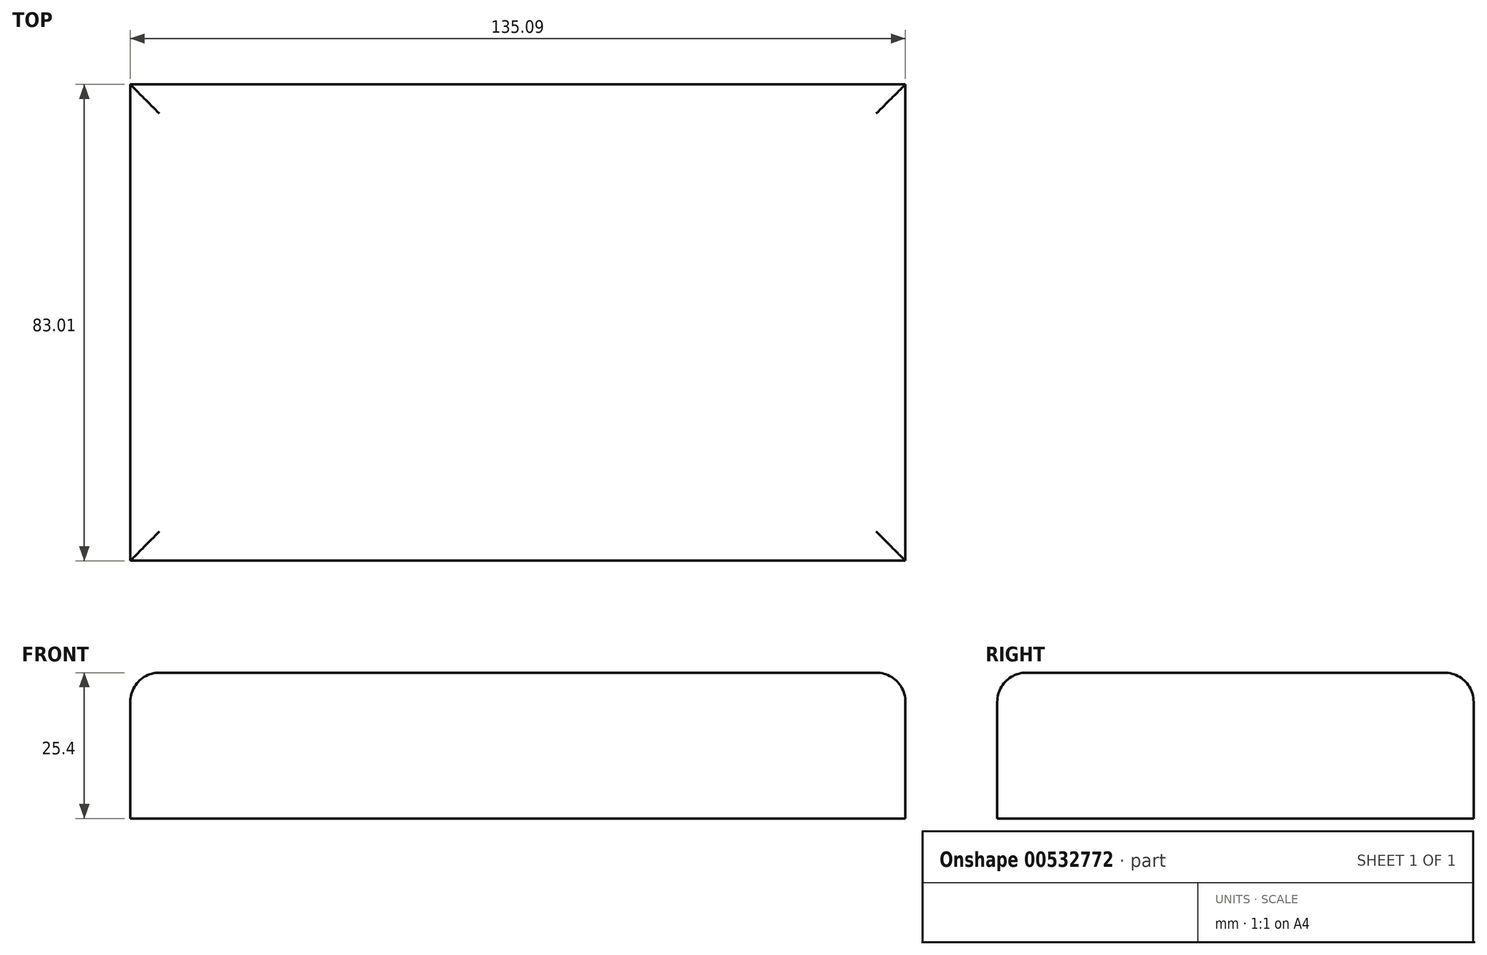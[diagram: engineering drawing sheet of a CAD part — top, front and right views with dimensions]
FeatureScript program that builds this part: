
annotation { "Feature Type Name" : "Feature", "Feature Type Description" : "" }
export const myFeature = defineFeature(function(context is Context, id is Id, definition is map)
    precondition{}
    {
        {
            var Q0;
            Q0=qCreatedBy(makeId("Top.planeOp"),FACE);
            var sketch = newSketch(context, id + "F0", { "sketchPlane" : qUnion([Q0])});
            skLineSegment(sketch, "E0.bottom", {"start": v(-66.21, -28.62) * mm, "end": v(68.88, -28.62) * mm});
            skLineSegment(sketch, "E0.top", {"start": v(-66.21, 54.4) * mm, "end": v(68.88, 54.4) * mm});
            skLineSegment(sketch, "E0.left", {"start": v(-66.21, -28.62) * mm, "end": v(-66.21, 54.4) * mm});
            skLineSegment(sketch, "E0.right", {"start": v(68.88, -28.62) * mm, "end": v(68.88, 54.4) * mm});
            skLineSegment(sketch, "E1.bottom", {"start": v(125.76, 181.67) * mm, "end": v(59.15, 181.67) * mm});
            skLineSegment(sketch, "E1.top", {"start": v(125.76, 162.43) * mm, "end": v(59.15, 162.43) * mm});
            skLineSegment(sketch, "E1.left", {"start": v(125.76, 181.67) * mm, "end": v(125.76, 162.43) * mm});
            skLineSegment(sketch, "E1.right", {"start": v(59.15, 181.67) * mm, "end": v(59.15, 162.43) * mm});
            skSolve(sketch);
        }
        {
            var Q0;
            Q0=makeQuery(id+"F0.imprint","IMPRINT",FACE,{"disambiguationData":[TD([[makeQuery(id+"F0.imprint","IMPRINT",EDGE,{"derivedFrom":sQuery(id+"F0.wireOp",EDGE,"E0.bottom")}),1.0]])]});
            extrude(context, id + "F1", {"entities" : qUnion([Q0]), "depth" : 25.4 * mm, "offsetDistance" : 25.4 * mm});
        }
        {
            var Q0;
            Q0=makeQuery(id+"F1.opExtrude","CAP_FACE",FACE,{"disambiguationData":[OSD([sQuery(id+"F0.wireOp",EDGE,"E0.bottom"),sQuery(id+"F0.wireOp",EDGE,"E0.top"),sQuery(id+"F0.wireOp",EDGE,"E0.left"),sQuery(id+"F0.wireOp",EDGE,"E0.right")])],"isStart":false});
            fillet(context, id + "F2", {"entities" : qUnion([Q0]), "radius" : 5.08 * mm, "tangentPropagation" : true, "allowEdgeOverflow" : false});
        }
    });
